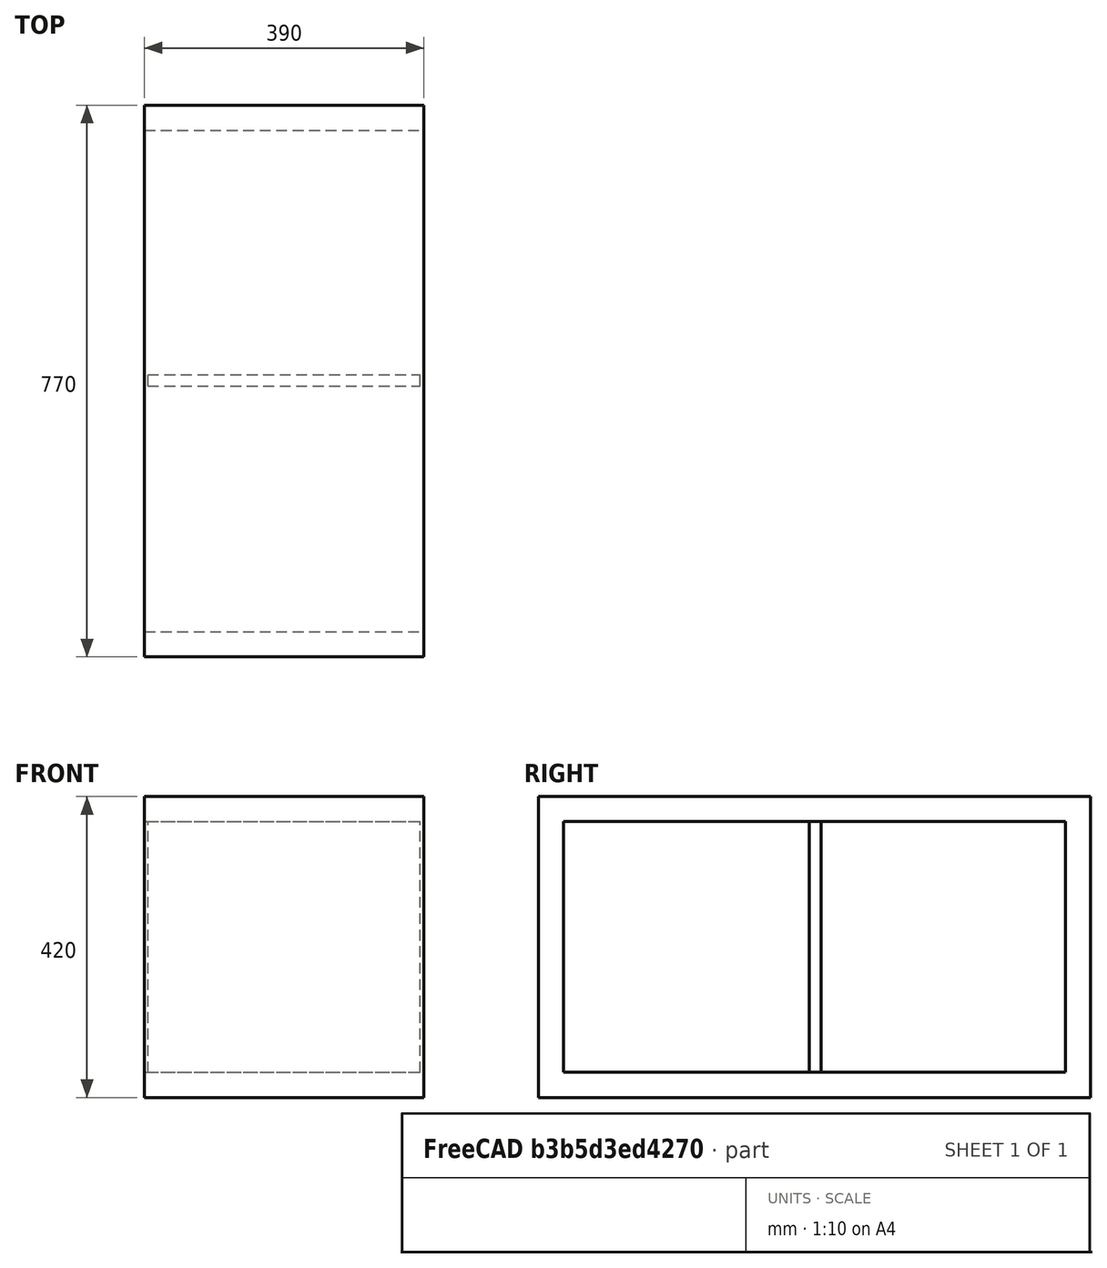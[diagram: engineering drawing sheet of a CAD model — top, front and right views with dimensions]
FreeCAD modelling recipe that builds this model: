
FCSTD DOCUMENT  (FreeCAD 0.18R16146 (Git))
Label: IKEA_Kallax_77x42cm
License: All rights reserved
LicenseURL: http://en.wikipedia.org/wiki/All_rights_reserved
objects: Part::Box×5, Part::MultiFuse×1
note: 6 computed .brp shape members not serialized (recipe doc carries the construction recipe); baked Part::Feature solids carry a one-line shape summary decoded from their .brp

FEATURE [Part::Box] Box  label="bottom"
  AttacherType = Attacher::AttachEngine3D
  Height = 35
  Length = 390
  Width = 770
FEATURE [Part::Box] Box001  label="side_left"
  AttacherType = Attacher::AttachEngine3D
  Height = 350
  Length = 390
  Placement = pos=(0,0,35) rot=(0,0,1;0rad)
  Width = 35
FEATURE [Part::Box] Box004  label="inner_separator"
  AttacherType = Attacher::AttachEngine3D
  Height = 350
  Length = 380
  Placement = pos=(5,378,35) rot=(0,0,1;0rad)
  Width = 16
FEATURE [Part::Box] Box005  label="side_right"
  AttacherType = Attacher::AttachEngine3D
  Height = 350
  Length = 390
  Placement = pos=(0,735,35) rot=(0,0,1;0rad)
  Width = 35
FEATURE [Part::Box] Box006  label="top"
  AttacherType = Attacher::AttachEngine3D
  Height = 35
  Length = 390
  Placement = pos=(0,0,385) rot=(0,0,1;0rad)
  Width = 770
FEATURE [Part::MultiFuse] Fusion  label="IKEA_Kallax_77x42cm"
  Shapes = -> [Box,Box006,Box004,Box001,Box005]
